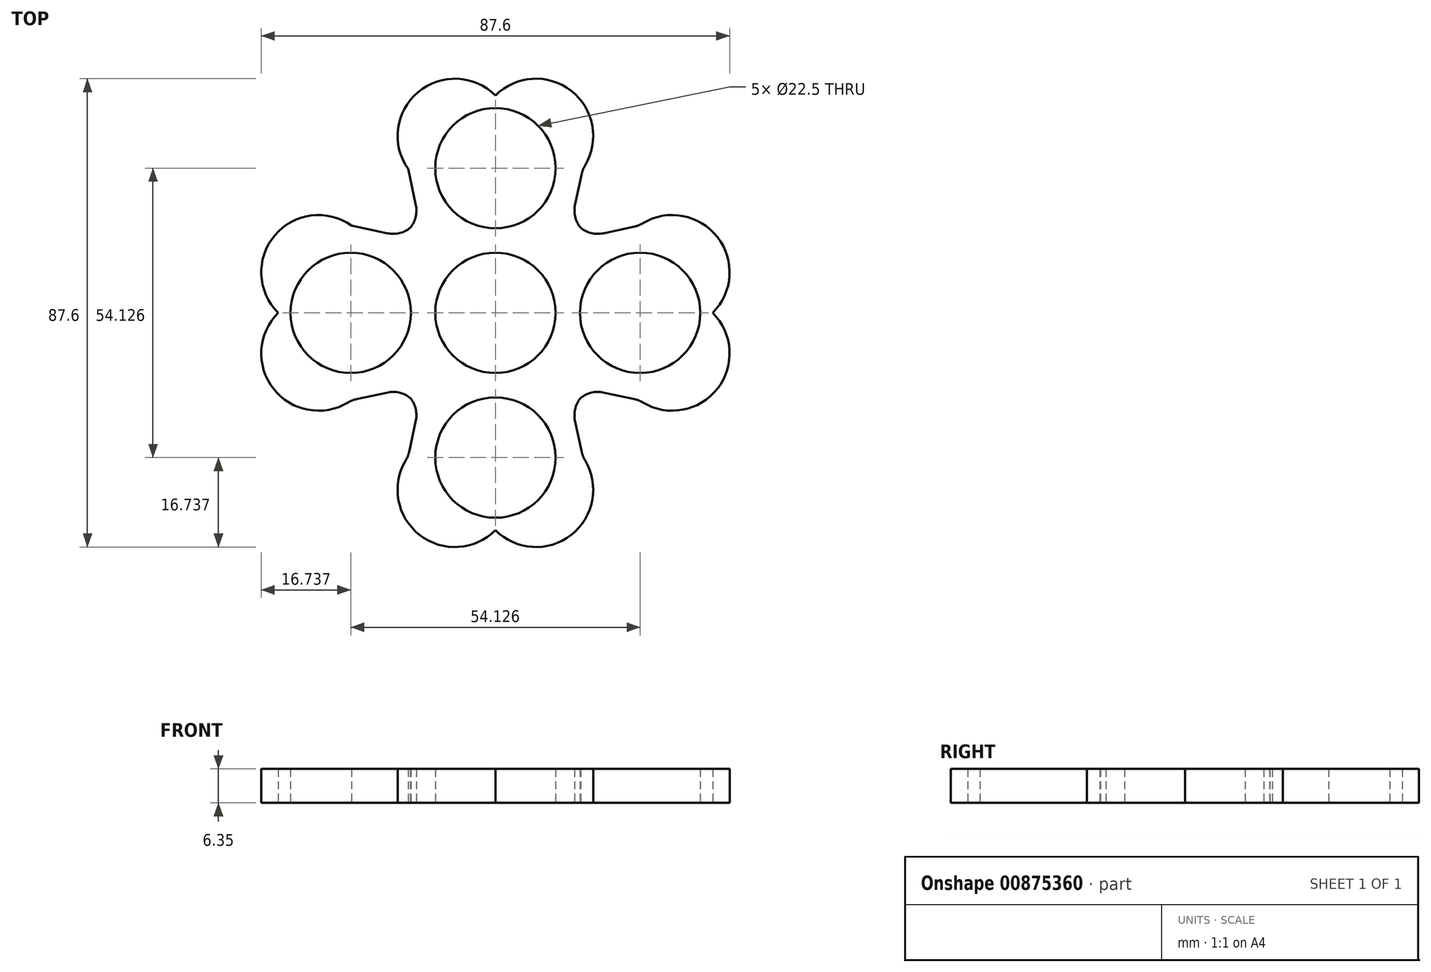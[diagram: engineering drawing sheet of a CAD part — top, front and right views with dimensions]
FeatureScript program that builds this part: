
annotation { "Feature Type Name" : "Feature", "Feature Type Description" : "" }
export const myFeature = defineFeature(function(context is Context, id is Id, definition is map)
    precondition{}
    {
        {
            var Q0;
            Q0=qCreatedBy(makeId("Top.planeOp"),FACE);
            var sketch = newSketch(context, id + "F0", { "sketchPlane" : qUnion([Q0])});
            skCircle(sketch, "E0", {"center": v(0, 0) * mm, "radius": 11.25 * mm});
            skCircle(sketch, "E1", {"center": v(0, 27.06) * mm, "radius": 11.25 * mm});
            skArc(sketch, "E2", {"start": v(-14.28, 17.39) * mm, "mid": v(-15.91, 15.91) * mm, "end": v(-17.39, 14.28) * mm});
            skArc(sketch, "E3", {"start": v(0, 40.64) * mm, "mid": v(-14.48, 41.28) * mm, "end": v(-16.33, 26.9) * mm});
            skLineSegment(sketch, "E4", {"start": v(-16.33, 26.9) * mm, "end": v(-14.28, 17.39) * mm});
            skArc(sketch, "E5.MirrorCS", {"start": v(0, 40.64) * mm, "mid": v(14.48, 41.28) * mm, "end": v(16.33, 26.9) * mm});
            skLineSegment(sketch, "E6.MirrorCS", {"start": v(16.33, 26.9) * mm, "end": v(14.28, 17.39) * mm});
            skArc(sketch, "E7.1.0", {"start": v(-40.64, 0) * mm, "mid": v(-41.28, -14.48) * mm, "end": v(-26.9, -16.33) * mm});
            skArc(sketch, "E7.1.1", {"start": v(-40.64, 0) * mm, "mid": v(-41.28, 14.48) * mm, "end": v(-26.9, 16.33) * mm});
            skLineSegment(sketch, "E7.1.2", {"start": v(-26.9, 16.33) * mm, "end": v(-17.39, 14.28) * mm});
            skLineSegment(sketch, "E7.1.3", {"start": v(-26.9, -16.33) * mm, "end": v(-17.39, -14.28) * mm});
            skCircle(sketch, "E7.1.4", {"center": v(-27.06, 0) * mm, "radius": 11.25 * mm});
            skArc(sketch, "E7.2.0", {"start": v(0, -40.64) * mm, "mid": v(14.48, -41.28) * mm, "end": v(16.33, -26.9) * mm});
            skArc(sketch, "E7.2.1", {"start": v(0, -40.64) * mm, "mid": v(-14.48, -41.28) * mm, "end": v(-16.33, -26.9) * mm});
            skLineSegment(sketch, "E7.2.2", {"start": v(-16.33, -26.9) * mm, "end": v(-14.28, -17.39) * mm});
            skLineSegment(sketch, "E7.2.3", {"start": v(16.33, -26.9) * mm, "end": v(14.28, -17.39) * mm});
            skCircle(sketch, "E7.2.4", {"center": v(0, -27.06) * mm, "radius": 11.25 * mm});
            skArc(sketch, "E8.3.3.0", {"start": v(40.64, 0) * mm, "mid": v(41.28, 14.48) * mm, "end": v(26.9, 16.33) * mm});
            skArc(sketch, "E8.4.3.0", {"start": v(40.64, 0) * mm, "mid": v(41.28, -14.48) * mm, "end": v(26.9, -16.33) * mm});
            skLineSegment(sketch, "E8.8.3.0", {"start": v(26.9, -16.33) * mm, "end": v(17.39, -14.28) * mm});
            skLineSegment(sketch, "E8.11.3.0", {"start": v(26.9, 16.33) * mm, "end": v(17.39, 14.28) * mm});
            skCircle(sketch, "E8.14.3.0", {"center": v(27.06, 0) * mm, "radius": 11.25 * mm});
            skArc(sketch, "E9.trimOffspring", {"start": v(-17.39, -14.28) * mm, "mid": v(-15.91, -15.91) * mm, "end": v(-14.28, -17.39) * mm});
            skArc(sketch, "E10.trimOffspring", {"start": v(14.28, -17.39) * mm, "mid": v(15.91, -15.91) * mm, "end": v(17.39, -14.28) * mm});
            skArc(sketch, "E11.trimOffspring", {"start": v(17.39, 14.28) * mm, "mid": v(15.91, 15.91) * mm, "end": v(14.28, 17.39) * mm});
            skSolve(sketch);
        }
        {
            var Q0;
            Q0=makeQuery(id+"F0.imprint","IMPRINT",FACE,{"disambiguationData":[TD([[makeQuery(id+"F0.imprint","IMPRINT",EDGE,{"derivedFrom":sQuery(id+"F0.wireOp",EDGE,"E0")}),-1.0]])]});
            var Q1;
            Q1=makeQuery(id+"F0.imprint","IMPRINT",FACE,{"disambiguationData":[TD([[makeQuery(id+"F0.imprint","IMPRINT",EDGE,{"derivedFrom":sQuery(id+"F0.wireOp",EDGE,"E7.1.0")}),1.0]])]});
            var Q2;
            Q2=makeQuery(id+"F0.imprint","IMPRINT",FACE,{"disambiguationData":[TD([[makeQuery(id+"F0.imprint","IMPRINT",EDGE,{"derivedFrom":sQuery(id+"F0.wireOp",EDGE,"E7.2.0")}),1.0]])]});
            var Q3;
            Q3=makeQuery(id+"F0.imprint","IMPRINT",FACE,{"disambiguationData":[TD([[makeQuery(id+"F0.imprint","IMPRINT",EDGE,{"derivedFrom":sQuery(id+"F0.wireOp",EDGE,"E8.3.3.0")}),1.0]])]});
            extrude(context, id + "F1", {"entities" : qUnion([Q0, Q1, Q2, Q3]), "depth" : 6.35 * mm, "offsetDistance" : 25.4 * mm});
        }
        {
            var Q0;
            Q0=makeQuery(id+"F1.opExtrude","SWEPT_EDGE",EDGE,{"disambiguationData":[OSD([sQuery(id+"F0.wireOp",EDGE,"E2"),sQuery(id+"F0.wireOp",EDGE,"E7.1.2")])]});
            var Q1;
            Q1=makeQuery(id+"F1.opExtrude","SWEPT_EDGE",EDGE,{"disambiguationData":[OSD([sQuery(id+"F0.wireOp",EDGE,"E2"),sQuery(id+"F0.wireOp",EDGE,"E4")])]});
            var Q2;
            Q2=makeQuery(id+"F1.opExtrude","SWEPT_EDGE",EDGE,{"disambiguationData":[OSD([sQuery(id+"F0.wireOp",EDGE,"E2"),sQuery(id+"F0.wireOp",EDGE,"E8.11.3.0")])]});
            var Q3;
            Q3=makeQuery(id+"F1.opExtrude","SWEPT_EDGE",EDGE,{"disambiguationData":[OSD([sQuery(id+"F0.wireOp",EDGE,"E2"),sQuery(id+"F0.wireOp",EDGE,"E6.MirrorCS")])]});
            var Q4;
            Q4=makeQuery(id+"F1.opExtrude","SWEPT_EDGE",EDGE,{"disambiguationData":[OSD([sQuery(id+"F0.wireOp",EDGE,"E2"),sQuery(id+"F0.wireOp",EDGE,"E7.2.3")])]});
            var Q5;
            Q5=makeQuery(id+"F1.opExtrude","SWEPT_EDGE",EDGE,{"disambiguationData":[OSD([sQuery(id+"F0.wireOp",EDGE,"E2"),sQuery(id+"F0.wireOp",EDGE,"E8.8.3.0")])]});
            var Q6;
            Q6=makeQuery(id+"F1.opExtrude","SWEPT_EDGE",EDGE,{"disambiguationData":[OSD([sQuery(id+"F0.wireOp",EDGE,"E2"),sQuery(id+"F0.wireOp",EDGE,"E7.1.3")])]});
            var Q7;
            Q7=makeQuery(id+"F1.opExtrude","SWEPT_EDGE",EDGE,{"disambiguationData":[OSD([sQuery(id+"F0.wireOp",EDGE,"E2"),sQuery(id+"F0.wireOp",EDGE,"E7.2.2")])]});
            fillet(context, id + "F2", {"entities" : qUnion([Q0, Q1, Q2, Q3, Q4, Q5, Q6, Q7]), "radius" : 5.08 * mm, "tangentPropagation" : true, "allowEdgeOverflow" : false});
        }
    });
